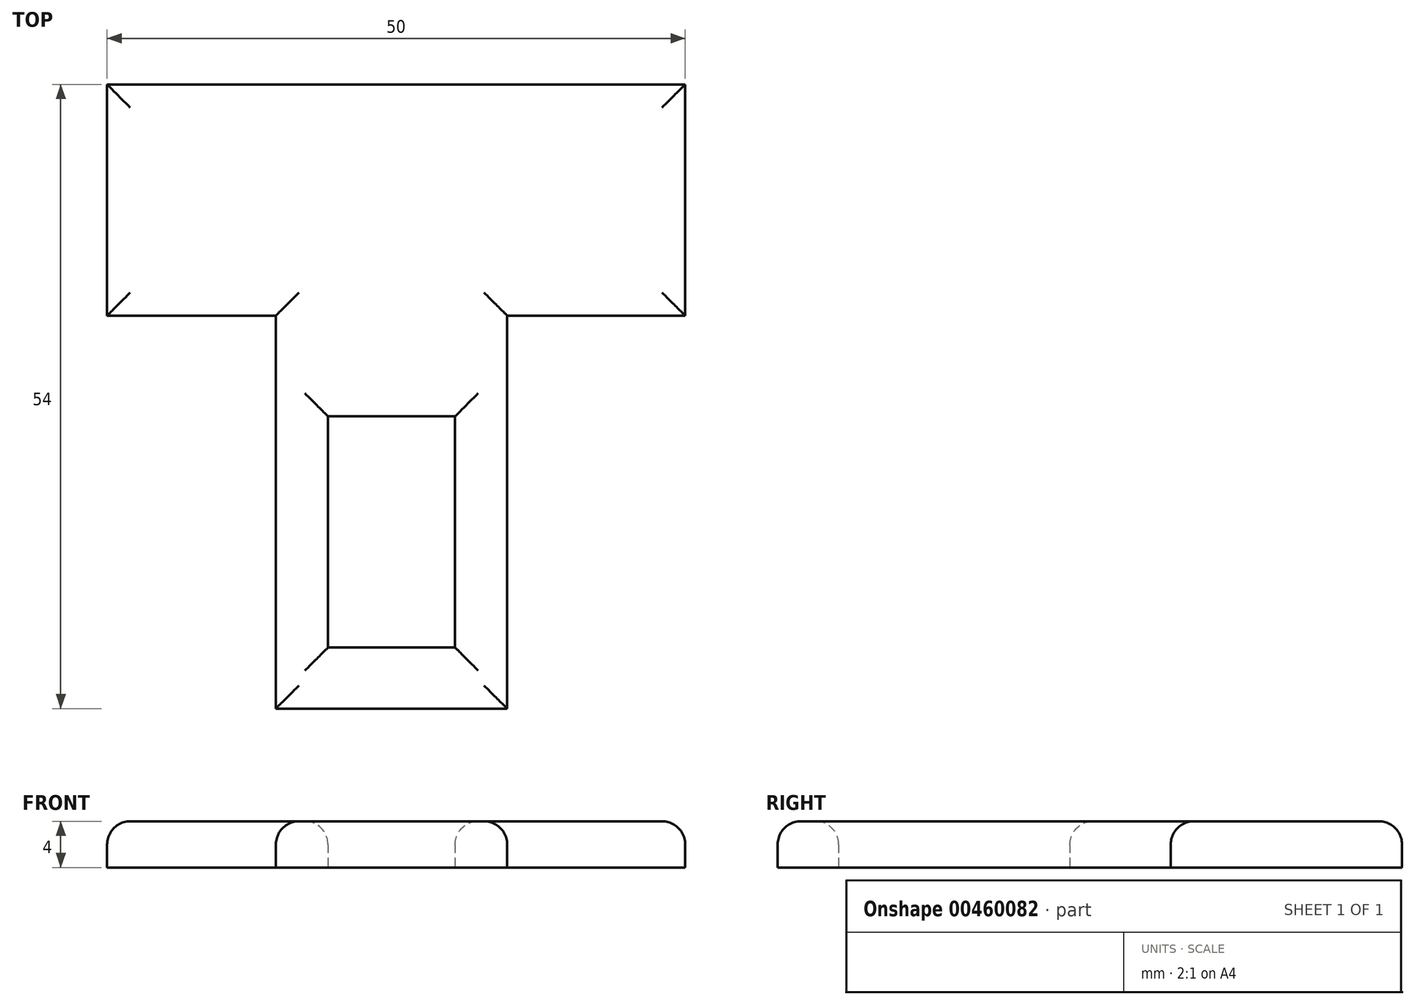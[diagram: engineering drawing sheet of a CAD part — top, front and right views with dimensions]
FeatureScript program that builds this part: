
annotation { "Feature Type Name" : "Feature", "Feature Type Description" : "" }
export const myFeature = defineFeature(function(context is Context, id is Id, definition is map)
    precondition{}
    {
        {
            var Q0;
            Q0=qCreatedBy(makeId("Top.planeOp"),FACE);
            var sketch = newSketch(context, id + "F0", { "sketchPlane" : qUnion([Q0])});
            skLineSegment(sketch, "E0.bottom", {"start": v(-10, -25.28) * mm, "end": v(10, -25.28) * mm});
            skLineSegment(sketch, "E0.top", {"start": v(-10, 25.28) * mm, "end": v(10, 25.28) * mm});
            skLineSegment(sketch, "E0.left", {"start": v(-10, -25.28) * mm, "end": v(-10, 25.28) * mm});
            skLineSegment(sketch, "E0.right", {"start": v(10, -25.28) * mm, "end": v(10, 25.28) * mm});
            skPoint(sketch, "E0.middle", {"position": v(0, 0) * mm});
            skLineSegment(sketch, "E1.bottom", {"start": v(-5.5, 0) * mm, "end": v(5.5, 0) * mm});
            skLineSegment(sketch, "E1.top", {"start": v(-5.5, -20) * mm, "end": v(5.5, -20) * mm});
            skLineSegment(sketch, "E1.left", {"start": v(-5.5, 0) * mm, "end": v(-5.5, -20) * mm});
            skLineSegment(sketch, "E1.right", {"start": v(5.5, 0) * mm, "end": v(5.5, -20) * mm});
            skLineSegment(sketch, "E2.bottom", {"start": v(-24.6, 28.72) * mm, "end": v(25.4, 28.72) * mm});
            skLineSegment(sketch, "E2.top", {"start": v(-24.6, 8.72) * mm, "end": v(25.4, 8.72) * mm});
            skLineSegment(sketch, "E2.left", {"start": v(-24.6, 28.72) * mm, "end": v(-24.6, 8.72) * mm});
            skLineSegment(sketch, "E2.right", {"start": v(25.4, 28.72) * mm, "end": v(25.4, 8.72) * mm});
            skSolve(sketch);
        }
        {
            var Q0;
            {var subQ1=sQuery(id+"F0.wireOp",EDGE,"E0.top");Q0=makeQuery(id+"F0.imprint","IMPRINT",FACE,{"disambiguationData":[TD([[makeQuery(id+"F0.imprint","IMPRINT",EDGE,{"derivedFrom":subQ1}),1.0]])]});}
            var Q1;
            {var subQ0=sQuery(id+"F0.wireOp",EDGE,"E0.top");Q1=makeQuery(id+"F0.imprint","IMPRINT",FACE,{"disambiguationData":[TD([[makeQuery(id+"F0.imprint","IMPRINT",EDGE,{"derivedFrom":subQ0}),-1.0]])]});}
            var Q2;
            {var subQ1=sQuery(id+"F0.wireOp",EDGE,"E0.bottom");Q2=makeQuery(id+"F0.imprint","IMPRINT",FACE,{"disambiguationData":[TD([[makeQuery(id+"F0.imprint","IMPRINT",EDGE,{"derivedFrom":subQ1}),1.0]])]});}
            extrude(context, id + "F1", {"entities" : qUnion([Q0, Q1, Q2]), "depth" : 4 * mm});
        }
        {
            var Q0;
            Q0=makeQuery(id+"F1.opExtrude","CAP_FACE",FACE,{"disambiguationData":[OSD([sQuery(id+"F0.wireOp",EDGE,"E0.bottom"),sQuery(id+"F0.wireOp",EDGE,"E0.left"),sQuery(id+"F0.wireOp",EDGE,"E0.right"),sQuery(id+"F0.wireOp",EDGE,"E1.bottom"),sQuery(id+"F0.wireOp",EDGE,"E1.top"),sQuery(id+"F0.wireOp",EDGE,"E1.left"),sQuery(id+"F0.wireOp",EDGE,"E1.right"),sQuery(id+"F0.wireOp",EDGE,"E2.bottom"),sQuery(id+"F0.wireOp",EDGE,"E2.top"),sQuery(id+"F0.wireOp",EDGE,"E2.left"),sQuery(id+"F0.wireOp",EDGE,"E2.right")])],"isStart":false});
            fillet(context, id + "F2", {"entities" : qUnion([Q0]), "radius" : 2 * mm, "tangentPropagation" : true, "allowEdgeOverflow" : false});
        }
    });
